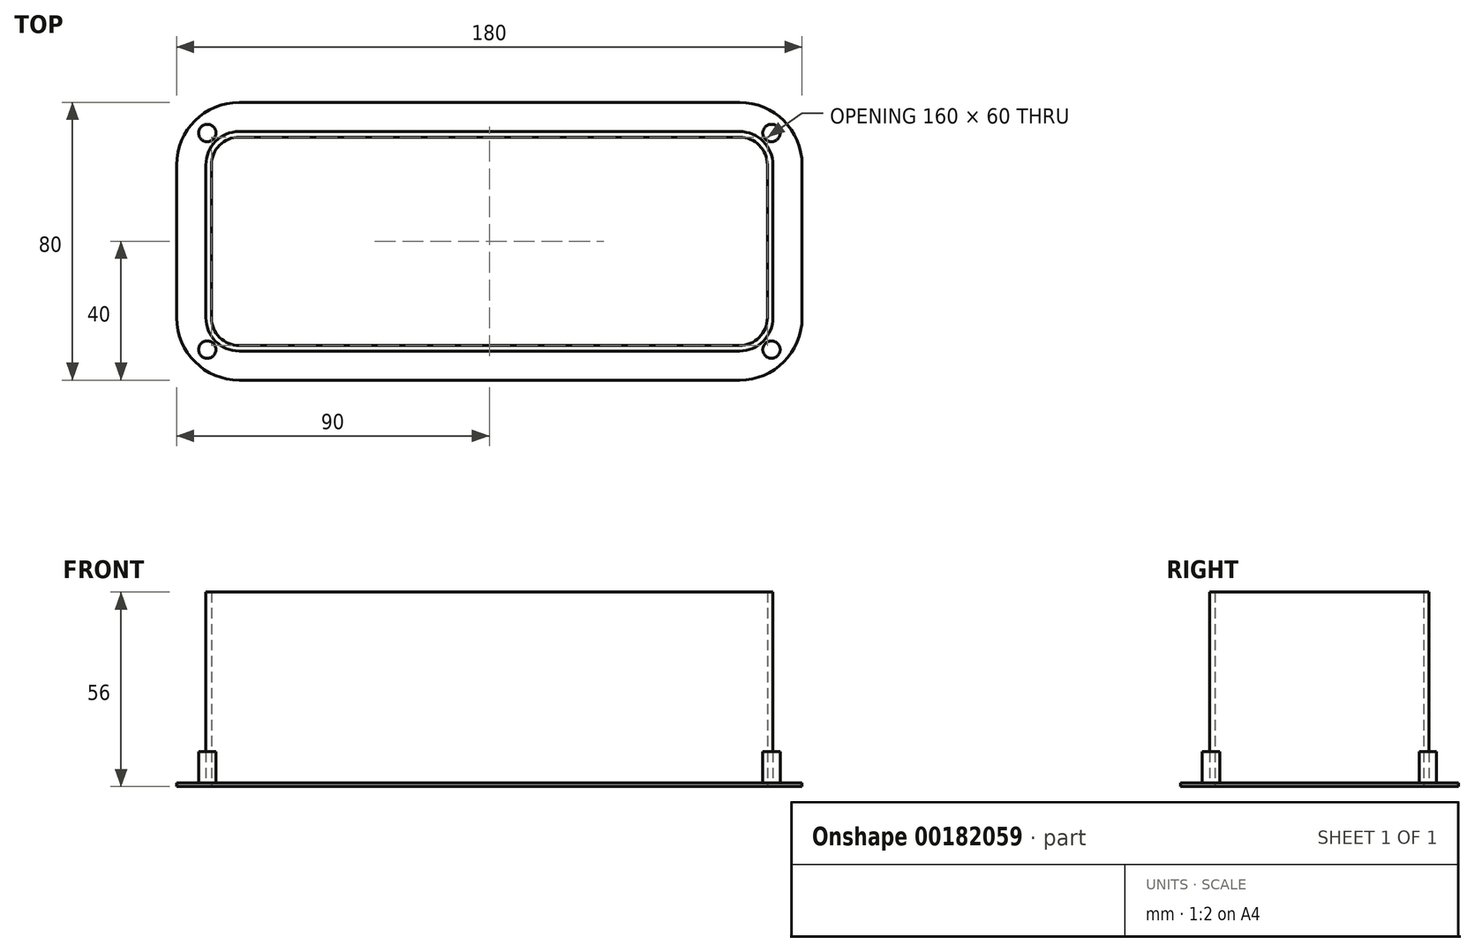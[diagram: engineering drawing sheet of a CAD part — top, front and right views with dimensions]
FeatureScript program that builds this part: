
annotation { "Feature Type Name" : "Feature", "Feature Type Description" : "" }
export const myFeature = defineFeature(function(context is Context, id is Id, definition is map)
    precondition{}
    {
        {
            var Q0;
            Q0=qCreatedBy(makeId("Top.planeOp"),FACE);
            var sketch = newSketch(context, id + "F0", { "sketchPlane" : qUnion([Q0])});
            skLineSegment(sketch, "E0.bottom", {"start": v(72, -40) * mm, "end": v(-72, -40) * mm});
            skLineSegment(sketch, "E0.top", {"start": v(72, 40) * mm, "end": v(-72, 40) * mm});
            skLineSegment(sketch, "E0.left", {"start": v(90, -22) * mm, "end": v(90, 22) * mm});
            skLineSegment(sketch, "E0.right", {"start": v(-90, -22) * mm, "end": v(-90, 22) * mm});
            skPoint(sketch, "E0.middle", {"position": v(0, 0) * mm});
            skPoint(sketch, "E1.visualSharp", {"position": v(-90, 40) * mm});
            skArc(sketch, "E1.filletArc", {"start": v(-72, 40) * mm, "mid": v(-84.73, 34.73) * mm, "end": v(-90, 22) * mm});
            skPoint(sketch, "E2.visualSharp", {"position": v(-90, -40) * mm});
            skArc(sketch, "E2.filletArc", {"start": v(-90, -22) * mm, "mid": v(-84.73, -34.73) * mm, "end": v(-72, -40) * mm});
            skPoint(sketch, "E3.visualSharp", {"position": v(90, -40) * mm});
            skArc(sketch, "E3.filletArc", {"start": v(72, -40) * mm, "mid": v(84.73, -34.73) * mm, "end": v(90, -22) * mm});
            skPoint(sketch, "E4.visualSharp", {"position": v(90, 40) * mm});
            skArc(sketch, "E4.filletArc", {"start": v(90, 22) * mm, "mid": v(84.73, 34.73) * mm, "end": v(72, 40) * mm});
            skLineSegment(sketch, "E5.0", {"start": v(72, 30) * mm, "end": v(-72, 30) * mm});
            skArc(sketch, "E5.1", {"start": v(80, 22) * mm, "mid": v(77.66, 27.66) * mm, "end": v(72, 30) * mm});
            skArc(sketch, "E5.2", {"start": v(-72, 30) * mm, "mid": v(-77.66, 27.66) * mm, "end": v(-80, 22) * mm});
            skLineSegment(sketch, "E5.3", {"start": v(80, -22) * mm, "end": v(80, 22) * mm});
            skLineSegment(sketch, "E5.4", {"start": v(-80, -22) * mm, "end": v(-80, 22) * mm});
            skArc(sketch, "E5.5", {"start": v(-80, -22) * mm, "mid": v(-77.66, -27.66) * mm, "end": v(-72, -30) * mm});
            skLineSegment(sketch, "E5.6", {"start": v(72, -30) * mm, "end": v(-72, -30) * mm});
            skArc(sketch, "E5.7", {"start": v(72, -30) * mm, "mid": v(77.66, -27.66) * mm, "end": v(80, -22) * mm});
            skSolve(sketch);
        }
        {
            var Q0;
            Q0=qSketchRegion(id+"F0",true);
            extrude(context, id + "F1", {"entities" : qUnion([Q0]), "depth" : 1 * mm});
        }
        {
            var Q0;
            Q0=makeQuery(id+"F1.opExtrude","CAP_FACE",FACE,{"disambiguationData":[OSD([sQuery(id+"F0.wireOp",EDGE,"E0.bottom"),sQuery(id+"F0.wireOp",EDGE,"E0.top"),sQuery(id+"F0.wireOp",EDGE,"E0.left"),sQuery(id+"F0.wireOp",EDGE,"E0.right"),sQuery(id+"F0.wireOp",EDGE,"E1.filletArc"),sQuery(id+"F0.wireOp",EDGE,"E2.filletArc"),sQuery(id+"F0.wireOp",EDGE,"E3.filletArc"),sQuery(id+"F0.wireOp",EDGE,"E4.filletArc"),sQuery(id+"F0.wireOp",EDGE,"E5.0"),sQuery(id+"F0.wireOp",EDGE,"E5.1"),sQuery(id+"F0.wireOp",EDGE,"E5.2"),sQuery(id+"F0.wireOp",EDGE,"E5.3"),sQuery(id+"F0.wireOp",EDGE,"E5.4"),sQuery(id+"F0.wireOp",EDGE,"E5.5"),sQuery(id+"F0.wireOp",EDGE,"E5.6"),sQuery(id+"F0.wireOp",EDGE,"E5.7")])],"isStart":false});
            var sketch = newSketch(context, id + "F2", { "sketchPlane" : qUnion([Q0])});
            skLineSegment(sketch, "E6.0", {"start": v(72, 30) * mm, "end": v(-72, 30) * mm});
            skArc(sketch, "E7.0", {"start": v(-72, 30) * mm, "mid": v(-77.66, 27.66) * mm, "end": v(-80, 22) * mm});
            skLineSegment(sketch, "E8.0", {"start": v(-80, -22) * mm, "end": v(-80, 22) * mm});
            skArc(sketch, "E9.0", {"start": v(-80, -22) * mm, "mid": v(-77.66, -27.66) * mm, "end": v(-72, -30) * mm});
            skLineSegment(sketch, "E10.0", {"start": v(72, -30) * mm, "end": v(-72, -30) * mm});
            skArc(sketch, "E11.0", {"start": v(72, -30) * mm, "mid": v(77.66, -27.66) * mm, "end": v(80, -22) * mm});
            skLineSegment(sketch, "E12.0", {"start": v(80, -22) * mm, "end": v(80, 22) * mm});
            skArc(sketch, "E13.0", {"start": v(80, 22) * mm, "mid": v(77.66, 27.66) * mm, "end": v(72, 30) * mm});
            skArc(sketch, "E14.0", {"start": v(81.6, 22) * mm, "mid": v(78.79, 28.79) * mm, "end": v(72, 31.6) * mm});
            skLineSegment(sketch, "E14.1", {"start": v(81.6, -22) * mm, "end": v(81.6, 22) * mm});
            skLineSegment(sketch, "E14.2", {"start": v(72, 31.6) * mm, "end": v(-72, 31.6) * mm});
            skArc(sketch, "E14.3", {"start": v(72, -31.6) * mm, "mid": v(78.79, -28.79) * mm, "end": v(81.6, -22) * mm});
            skArc(sketch, "E14.4", {"start": v(-72, 31.6) * mm, "mid": v(-78.79, 28.79) * mm, "end": v(-81.6, 22) * mm});
            skLineSegment(sketch, "E14.5", {"start": v(-81.6, -22) * mm, "end": v(-81.6, 22) * mm});
            skArc(sketch, "E14.6", {"start": v(-81.6, -22) * mm, "mid": v(-78.79, -28.79) * mm, "end": v(-72, -31.6) * mm});
            skLineSegment(sketch, "E14.7", {"start": v(72, -31.6) * mm, "end": v(-72, -31.6) * mm});
            skArc(sketch, "E15.0", {"start": v(-85, -22) * mm, "mid": v(-81.2, -31.2) * mm, "end": v(-72, -35) * mm});
            skLineSegment(sketch, "E15.1", {"start": v(-85, 22) * mm, "end": v(-85, -22) * mm});
            skLineSegment(sketch, "E15.2", {"start": v(-72, -35) * mm, "end": v(72, -35) * mm});
            skArc(sketch, "E15.3", {"start": v(-72, 35) * mm, "mid": v(-81.2, 31.2) * mm, "end": v(-85, 22) * mm});
            skArc(sketch, "E15.4", {"start": v(72, -35) * mm, "mid": v(81.2, -31.2) * mm, "end": v(85, -22) * mm});
            skLineSegment(sketch, "E15.5", {"start": v(85, -22) * mm, "end": v(85, 22) * mm});
            skArc(sketch, "E15.6", {"start": v(85, 22) * mm, "mid": v(81.2, 31.2) * mm, "end": v(72, 35) * mm});
            skLineSegment(sketch, "E15.7", {"start": v(72, 35) * mm, "end": v(-72, 35) * mm});
            skSolve(sketch);
        }
        {
            var Q0;
            Q0=makeQuery(id+"F2.imprint","IMPRINT",FACE,{"disambiguationData":[TD([[makeQuery(id+"F2.imprint","IMPRINT",EDGE,{"derivedFrom":sQuery(id+"F2.wireOp",EDGE,"E6.0")}),-1.0]])]});
            extrude(context, id + "F3", {"entities" : qUnion([Q0]), "operationType" : NewBodyOperationType.ADD, "depth" : 55 * mm});
        }
        {
            var Q0;
            Q0=makeQuery(id+"F1.opExtrude","CAP_FACE",FACE,{"disambiguationData":[OSD([sQuery(id+"F0.wireOp",EDGE,"E0.bottom"),sQuery(id+"F0.wireOp",EDGE,"E0.top"),sQuery(id+"F0.wireOp",EDGE,"E0.left"),sQuery(id+"F0.wireOp",EDGE,"E0.right"),sQuery(id+"F0.wireOp",EDGE,"E1.filletArc"),sQuery(id+"F0.wireOp",EDGE,"E2.filletArc"),sQuery(id+"F0.wireOp",EDGE,"E3.filletArc"),sQuery(id+"F0.wireOp",EDGE,"E4.filletArc"),sQuery(id+"F0.wireOp",EDGE,"E5.0"),sQuery(id+"F0.wireOp",EDGE,"E5.1"),sQuery(id+"F0.wireOp",EDGE,"E5.2"),sQuery(id+"F0.wireOp",EDGE,"E5.3"),sQuery(id+"F0.wireOp",EDGE,"E5.4"),sQuery(id+"F0.wireOp",EDGE,"E5.5"),sQuery(id+"F0.wireOp",EDGE,"E5.6"),sQuery(id+"F0.wireOp",EDGE,"E5.7")])],"isStart":true});
            var sketch = newSketch(context, id + "F4", { "sketchPlane" : qUnion([Q0])});
            skLineSegment(sketch, "E16", {"start": v(-77.66, -27.66) * mm, "end": v(-84.73, -34.73) * mm});
            skLineSegment(sketch, "E17", {"start": v(77.66, -27.66) * mm, "end": v(84.73, -34.73) * mm});
            skLineSegment(sketch, "E18", {"start": v(77.66, 27.66) * mm, "end": v(84.73, 34.73) * mm});
            skLineSegment(sketch, "E19", {"start": v(-77.66, 27.66) * mm, "end": v(-84.73, 34.73) * mm});
            skCircle(sketch, "E20", {"center": v(81.2, -31.2) * mm, "radius": 2.5 * mm});
            skCircle(sketch, "E21", {"center": v(-81.2, -31.2) * mm, "radius": 2.5 * mm});
            skCircle(sketch, "E22", {"center": v(81.2, 31.2) * mm, "radius": 2.5 * mm});
            skCircle(sketch, "E23", {"center": v(-81.2, 31.2) * mm, "radius": 2.5 * mm});
            skSolve(sketch);
        }
        {
            var Q0;
            Q0=qSketchRegion(id+"F4",true);
            extrude(context, id + "F5", {"entities" : qUnion([Q0]), "operationType" : NewBodyOperationType.ADD, "oppositeDirection" : true, "depth" : 10 * mm});
        }
    });
